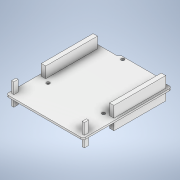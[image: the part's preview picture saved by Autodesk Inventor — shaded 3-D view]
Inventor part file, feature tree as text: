
AUTODESK INVENTOR PART (.ipt)
format: ipt  version: 2022 (Build 260153000, 153)  size: 204,288 bytes
history: native  units: mm
features: extrude x4, sketch x4, fillet x1
ambient origin geometry x8: Origin, YZ Plane, XZ Plane, XY Plane, X Axis, Y Axis, Z Axis, Center Point
bodies: Solid1 (feature_tree)
feature tree (9):
  extrude  "Extrusion1"  Depth=80.5mm
  fillet  "Fillet1"  Radius=20.51mm
  extrude  "Extrusion2"  Depth=80.5mm
  extrude  "Extrusion3"  TaperAngle=45.0deg  [1 undecoded]
  extrude  "Extrusion4"  Depth=1.65mm TaperAngle=0.0deg
  sketch  "Sketch1"  dims[d0=70.0mm d1=80.5mm d2=20.51mm]
  sketch  "Sketch2"  dims[d3=80.5mm d4=11.33mm]
  sketch  "Sketch3"  dims[d5=82.45mm d6=45.0deg]
  sketch  "Sketch4"  dims[d7=45.0deg d8=1.65mm d9=0.0mm d10=2.0mm d11=3.0mm d12=3.0mm d13=3.0mm d14=29.0mm d15=10.5mm d16=10.5mm d17=2.3mm d18=25.8mm d19=20.0mm d20=0.0mm d21=4.0mm d22=47.0mm d23=30.0mm d24=2.0mm d27=2.0mm d28=4.0mm d30=30.0mm d31=8.3mm d32=0.0mm d33=2.0mm d34=4.0mm d35=2.0mm d36=4.0mm d37=3.0mm d38=10.0mm d39=0.0mm d40=27.7mm]
note: 1 required parameter value undecoded (feature->parameter linkage not recoverable at this tier; creation-order binding heuristic only, values carry confidence <= 0.55)
